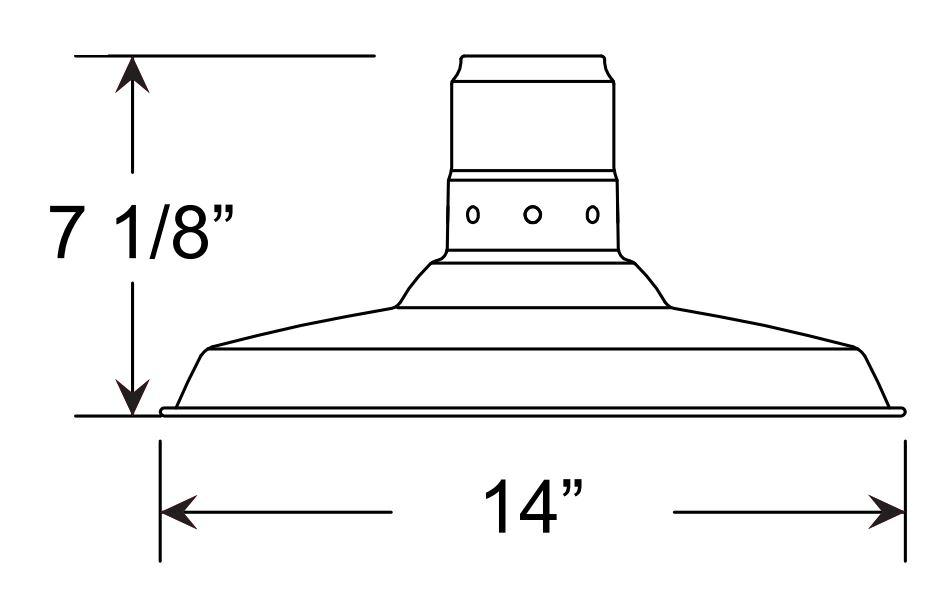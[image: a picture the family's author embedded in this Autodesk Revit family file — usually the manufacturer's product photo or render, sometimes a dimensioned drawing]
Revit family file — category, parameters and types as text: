
# Revit family: BISTRO(8,12,14,16,18) MB
name_source: partatom
category: Lighting Fixtures
units: mm (PartAtom-declared; Revit-internal decimal feet)

## family parameters
Always vertical = Yes
Cut with Voids When Loaded = No
Light Source = Yes
OmniClass Number = 23.80.70.00
OmniClass Title = Lighting
Part Type = Normal
Room Calculation Point = No
Round Connector Dimension = Use Diameter
Shared = No
Work Plane-Based = No

## types (5) — shared parameters
Body Colour = Spun aluminium
Body Material = body
CRI = >90
Color Filter = 16777215
Construction Material = Heavy Duty spun aluminum.
Default Elevation = 0' - 0"
Description = 120-277 Voltage
Dimming = 1%
Dimming Lamp Color Temperature Shift = <None>
Efficiency = 65-125 lumens per watt
Lamp = MB
Life = L70 50,000 hours
Load Classification = Lighting
Manufacturer = ANP Lighting
Photometric Web File = BB14-100GLCL-32WPL.ies
Power Factor = 1
Tilt Angle = 90.00°
URL = https://www.anplighting.com
Voltage = 277 V
Warranty = 5 year limited warranty

## per-type parameters (varying)
| type | Apparent Load | BB08 | BB12 | BB14 | BB16 | BB18 | Fixture Diameter | Fixture Height | Model | Wattage Comments | Weight |
| BB08 | 100 VA | Yes | No | No | No | No | 0' - 8" | 0' - 6" | BB 08 | 100W Max | 1 lbs |
| BB12 | 100 VA | No | Yes | No | No | No | 1' - 0" | 0' - 8 1/2" | BB 12 | 100W Max | 1.5 lbs |
| BB14 | 200 VA | No | No | Yes | No | No | 1' - 2" | 0' - 10" | BB 14 | 200W Max | 1.5 lbs |
| BB16 | 200 VA | No | No | No | Yes | No | 1' - 4" | 0' - 10" | BB 16 | 200W Max | 1.5 lbs |
| BB18 | 200 VA | No | No | No | No | Yes | 1' - 6" | 0' - 11" | BB 18 | 200W Max | 2.5 lbs |

## geometry (parser evidence)
native form markers: Sweep x35
no freeform markers — native parametric forms only
